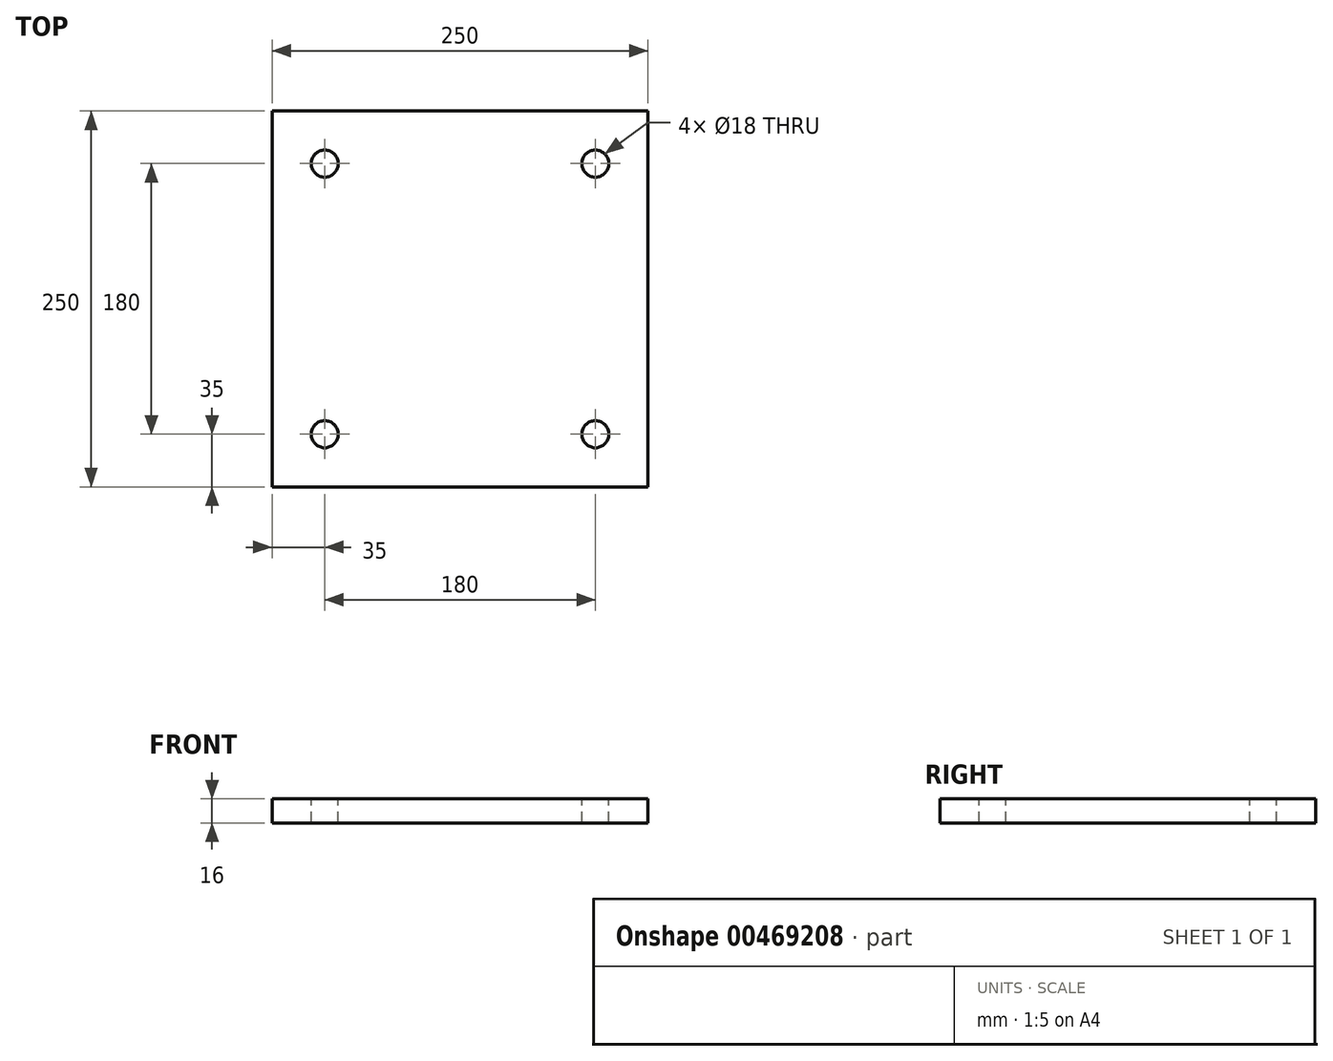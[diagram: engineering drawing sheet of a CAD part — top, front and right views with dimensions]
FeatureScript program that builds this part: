
annotation { "Feature Type Name" : "Feature", "Feature Type Description" : "" }
export const myFeature = defineFeature(function(context is Context, id is Id, definition is map)
    precondition{}
    {
        {
            var Q0;
            Q0=qCreatedBy(makeId("Top.planeOp"),FACE);
            var sketch = newSketch(context, id + "F0", { "sketchPlane" : qUnion([Q0])});
            skLineSegment(sketch, "E0.bottom", {"start": v(125, 125) * mm, "end": v(-125, 125) * mm});
            skLineSegment(sketch, "E0.top", {"start": v(125, -125) * mm, "end": v(-125, -125) * mm});
            skLineSegment(sketch, "E0.left", {"start": v(125, 125) * mm, "end": v(125, -125) * mm});
            skLineSegment(sketch, "E0.right", {"start": v(-125, 125) * mm, "end": v(-125, -125) * mm});
            skPoint(sketch, "E0.middle", {"position": v(0, 0) * mm});
            skSolve(sketch);
        }
        {
            var Q0;
            Q0=qSketchRegion(id+"F0",true);
            extrude(context, id + "F1", {"entities" : qUnion([Q0]), "depth" : 16 * mm});
        }
        {
            var Q0;
            Q0=makeQuery(id+"F1.opExtrude","CAP_FACE",FACE,{"disambiguationData":[OSD([sQuery(id+"F0.wireOp",EDGE,"E0.bottom"),sQuery(id+"F0.wireOp",EDGE,"E0.top"),sQuery(id+"F0.wireOp",EDGE,"E0.left"),sQuery(id+"F0.wireOp",EDGE,"E0.right")])],"isStart":false});
            var sketch = newSketch(context, id + "F2", { "sketchPlane" : qUnion([Q0])});
            skPoint(sketch, "E1", {"position": v(-90, 90) * mm});
            skPoint(sketch, "E2", {"position": v(90, 90) * mm});
            skPoint(sketch, "E3", {"position": v(90, -90) * mm});
            skPoint(sketch, "E4", {"position": v(-90, -90) * mm});
            skSolve(sketch);
        }
        {
            var Q0;
            Q0=sQuery(id+"F2.wireOp",VERTEX,"E1");
            var Q1;
            Q1=sQuery(id+"F2.wireOp",VERTEX,"E2");
            var Q2;
            Q2=sQuery(id+"F2.wireOp",VERTEX,"E3");
            var Q3;
            Q3=sQuery(id+"F2.wireOp",VERTEX,"E4");
            var Q4;
            Q4=makeQuery(id+"F1.opExtrude","SWEPT_BODY",BODY,{"disambiguationData":[OSD([sQuery(id+"F0.wireOp",EDGE,"E0.bottom"),sQuery(id+"F0.wireOp",EDGE,"E0.top"),sQuery(id+"F0.wireOp",EDGE,"E0.left"),sQuery(id+"F0.wireOp",EDGE,"E0.right")])]});
            hole(context, id + "F3", {"style" : HoleStyle.SIMPLE, "endStyle" : HoleEndStyle.BLIND, "holeDiameter" : 18 * mm, "holeDepth" : 20 * mm, "isTappedThrough" : true, "tappedDepth" : 12 * mm, "tapClearance" : 3, "startFromSketch" : true, "locations" : qUnion([Q0, Q1, Q2, Q3]), "scope" : qUnion([Q4])});
        }
    });
